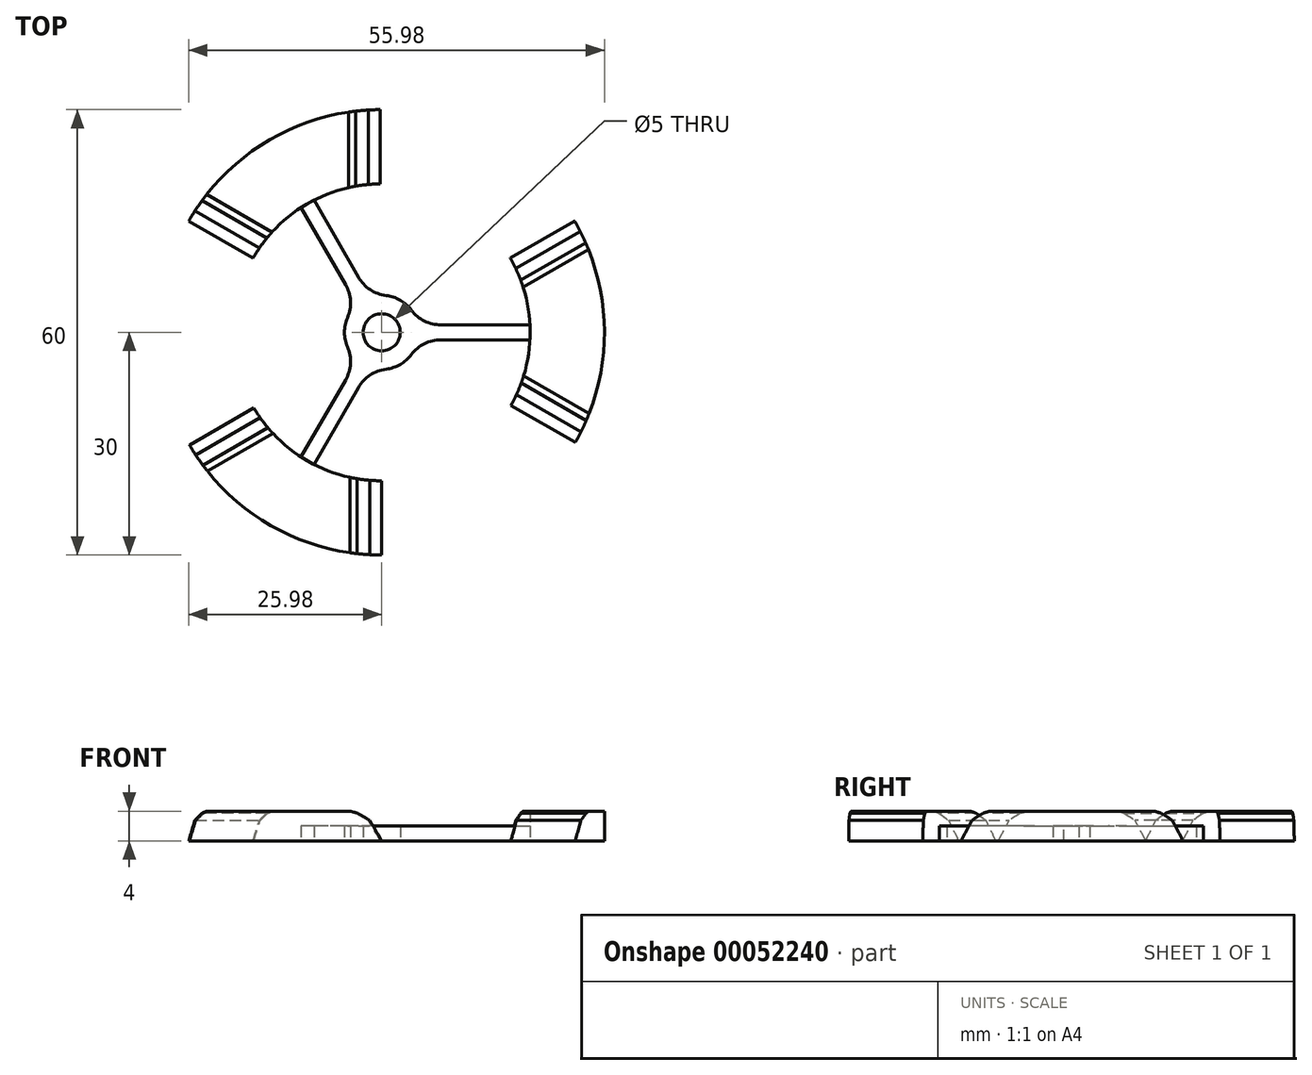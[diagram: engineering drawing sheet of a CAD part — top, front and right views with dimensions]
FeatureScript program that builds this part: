
annotation { "Feature Type Name" : "Feature", "Feature Type Description" : "" }
export const myFeature = defineFeature(function(context is Context, id is Id, definition is map)
    precondition{}
    {
        {
            var Q0;
            Q0=qCreatedBy(makeId("Top.planeOp"),FACE);
            var sketch = newSketch(context, id + "F0", { "sketchPlane" : qUnion([Q0])});
            skCircle(sketch, "E0", {"center": v(0, 0) * mm, "radius": 30 * mm});
            skCircle(sketch, "E1", {"center": v(0, 0) * mm, "radius": 20 * mm});
            skLineSegment(sketch, "E2", {"start": v(0, 20) * mm, "end": v(0, 30) * mm});
            skLineSegment(sketch, "E3", {"start": v(-17.32, -10) * mm, "end": v(-25.98, -15) * mm});
            skLineSegment(sketch, "E4", {"start": v(17.32, -10) * mm, "end": v(25.98, -15) * mm});
            skLineSegment(sketch, "E5", {"start": v(0, -20) * mm, "end": v(0, -30) * mm});
            skLineSegment(sketch, "E6", {"start": v(-17.32, 10) * mm, "end": v(-25.98, 15) * mm});
            skLineSegment(sketch, "E7", {"start": v(17.32, 10) * mm, "end": v(25.98, 15) * mm});
            skLineSegment(sketch, "E8", {"start": v(0, 0) * mm, "end": v(-10, 17.32) * mm, "construction": true});
            skLineSegment(sketch, "E9", {"start": v(0, 0) * mm, "end": v(-10, -17.32) * mm, "construction": true});
            skLineSegment(sketch, "E10", {"start": v(0, 0) * mm, "end": v(20, 0) * mm, "construction": true});
            skCircle(sketch, "E11", {"center": v(0, 0) * mm, "radius": 5 * mm});
            skLineSegment(sketch, "E12.0", {"start": v(-1.58, 4.74) * mm, "end": v(-9.12, 17.8) * mm});
            skLineSegment(sketch, "E13.MirrorCS", {"start": v(-3.32, 3.74) * mm, "end": v(-10.85, 16.8) * mm});
            skLineSegment(sketch, "E14.0", {"start": v(-3.32, -3.74) * mm, "end": v(-10.87, -16.82) * mm});
            skLineSegment(sketch, "E15.MirrorCS", {"start": v(-1.58, -4.74) * mm, "end": v(-9.13, -17.82) * mm});
            skLineSegment(sketch, "E16.0", {"start": v(4.9, -1) * mm, "end": v(20, -1) * mm});
            skLineSegment(sketch, "E17.MirrorCS", {"start": v(4.9, 1) * mm, "end": v(20, 1) * mm});
            skCircle(sketch, "E18", {"center": v(0, 0) * mm, "radius": 2.5 * mm});
            skSolve(sketch);
        }
        {
            var Q0;
            {var subQ0=sQuery(id+"F0.wireOp",EDGE,"E14.0");var subQ1=sQuery(id+"F0.wireOp",EDGE,"E1");var subQ2=makeQuery(id+"F0.imprint","INTERSECT",VERTEX,{"derivedFrom":[subQ1,subQ0]});Q0=makeQuery(id+"F0.imprint","IMPRINT",FACE,{"disambiguationData":[TD([[makeQuery(id+"F0.imprint","IMPRINT",EDGE,{"disambiguationData":[TD([[subQ2,-1.0]])],"derivedFrom":subQ1}),1.0]])]});}
            var Q1;
            {var subQ0=sQuery(id+"F0.wireOp",EDGE,"E12.0");Q1=makeQuery(id+"F0.imprint","IMPRINT",FACE,{"disambiguationData":[TD([[makeQuery(id+"F0.imprint","IMPRINT",EDGE,{"derivedFrom":subQ0}),1.0]])]});}
            var Q2;
            {var subQ0=sQuery(id+"F0.wireOp",EDGE,"E17.MirrorCS");var subQ1=sQuery(id+"F0.wireOp",EDGE,"E1");var subQ2=makeQuery(id+"F0.imprint","INTERSECT",VERTEX,{"derivedFrom":[subQ1,subQ0]});Q2=makeQuery(id+"F0.imprint","IMPRINT",FACE,{"disambiguationData":[TD([[makeQuery(id+"F0.imprint","IMPRINT",EDGE,{"disambiguationData":[TD([[subQ2,1.0]])],"derivedFrom":subQ1}),1.0]])]});}
            var Q3;
            {var subQ0=sQuery(id+"F0.wireOp",EDGE,"E11");var subQ4=makeQuery(id+"F0.imprint","INTERSECT",VERTEX,{"derivedFrom":[subQ0,sQuery(id+"F0.wireOp",EDGE,"E12.0")]});Q3=makeQuery(id+"F0.imprint","IMPRINT",FACE,{"disambiguationData":[TD([[makeQuery(id+"F0.imprint","IMPRINT",EDGE,{"disambiguationData":[TD([[subQ4,1.0]])],"derivedFrom":subQ0}),1.0]])]});}
            extrude(context, id + "F1", {"entities" : qUnion([Q0, Q1, Q2, Q3]), "depth" : 2 * mm});
        }
        {
            var Q0;
            {var subQ4=sQuery(id+"F0.wireOp",EDGE,"E2");Q0=makeQuery(id+"F0.imprint","IMPRINT",FACE,{"disambiguationData":[TD([[makeQuery(id+"F0.imprint","IMPRINT",EDGE,{"derivedFrom":subQ4}),1.0]])]});}
            var Q1;
            {var subQ4=sQuery(id+"F0.wireOp",EDGE,"E4");Q1=makeQuery(id+"F0.imprint","IMPRINT",FACE,{"disambiguationData":[TD([[makeQuery(id+"F0.imprint","IMPRINT",EDGE,{"derivedFrom":subQ4}),1.0]])]});}
            var Q2;
            {var subQ4=sQuery(id+"F0.wireOp",EDGE,"E3");Q2=makeQuery(id+"F0.imprint","IMPRINT",FACE,{"disambiguationData":[TD([[makeQuery(id+"F0.imprint","IMPRINT",EDGE,{"derivedFrom":subQ4}),1.0]])]});}
            extrude(context, id + "F2", {"entities" : qUnion([Q0, Q1, Q2]), "operationType" : NewBodyOperationType.ADD, "depth" : 4 * mm});
        }
        {
            var Q0;
            Q0=makeQuery(id+"F1.opExtrude","SWEPT_EDGE",EDGE,{"disambiguationData":[OSD([sQuery(id+"F0.wireOp",EDGE,"E1"),sQuery(id+"F0.wireOp",EDGE,"E12.0")])]});
            var Q1;
            Q1=makeQuery(id+"F1.opExtrude","SWEPT_EDGE",EDGE,{"disambiguationData":[OSD([sQuery(id+"F0.wireOp",EDGE,"E1"),sQuery(id+"F0.wireOp",EDGE,"E13.MirrorCS")])]});
            var Q2;
            Q2=makeQuery(id+"F1.opExtrude","SWEPT_EDGE",EDGE,{"disambiguationData":[OSD([sQuery(id+"F0.wireOp",EDGE,"E1"),sQuery(id+"F0.wireOp",EDGE,"E17.MirrorCS")])]});
            var Q3;
            Q3=makeQuery(id+"F1.opExtrude","SWEPT_EDGE",EDGE,{"disambiguationData":[OSD([sQuery(id+"F0.wireOp",EDGE,"E1"),sQuery(id+"F0.wireOp",EDGE,"E16.0")])]});
            var Q4;
            Q4=makeQuery(id+"F1.opExtrude","SWEPT_EDGE",EDGE,{"disambiguationData":[OSD([sQuery(id+"F0.wireOp",EDGE,"E1"),sQuery(id+"F0.wireOp",EDGE,"E14.0")])]});
            var Q5;
            Q5=makeQuery(id+"F1.opExtrude","SWEPT_EDGE",EDGE,{"disambiguationData":[OSD([sQuery(id+"F0.wireOp",EDGE,"E1"),sQuery(id+"F0.wireOp",EDGE,"E15.MirrorCS")])]});
            var Q6;
            Q6=makeQuery(id+"F1.opExtrude","SWEPT_EDGE",EDGE,{"disambiguationData":[OSD([sQuery(id+"F0.wireOp",EDGE,"E11"),sQuery(id+"F0.wireOp",EDGE,"E12.0")])]});
            var Q7;
            Q7=makeQuery(id+"F1.opExtrude","SWEPT_EDGE",EDGE,{"disambiguationData":[OSD([sQuery(id+"F0.wireOp",EDGE,"E11"),sQuery(id+"F0.wireOp",EDGE,"E17.MirrorCS")])]});
            var Q8;
            Q8=makeQuery(id+"F1.opExtrude","SWEPT_EDGE",EDGE,{"disambiguationData":[OSD([sQuery(id+"F0.wireOp",EDGE,"E11"),sQuery(id+"F0.wireOp",EDGE,"E13.MirrorCS")])]});
            var Q9;
            Q9=makeQuery(id+"F1.opExtrude","SWEPT_EDGE",EDGE,{"disambiguationData":[OSD([sQuery(id+"F0.wireOp",EDGE,"E11"),sQuery(id+"F0.wireOp",EDGE,"E14.0")])]});
            var Q10;
            Q10=makeQuery(id+"F1.opExtrude","SWEPT_EDGE",EDGE,{"disambiguationData":[OSD([sQuery(id+"F0.wireOp",EDGE,"E11"),sQuery(id+"F0.wireOp",EDGE,"E15.MirrorCS")])]});
            var Q11;
            Q11=makeQuery(id+"F1.opExtrude","SWEPT_EDGE",EDGE,{"disambiguationData":[OSD([sQuery(id+"F0.wireOp",EDGE,"E11"),sQuery(id+"F0.wireOp",EDGE,"E16.0")])]});
            fillet(context, id + "F3", {"entities" : qUnion([Q0, Q1, Q2, Q3, Q4, Q5, Q6, Q7, Q8, Q9, Q10, Q11]), "radius" : 5 * mm, "tangentPropagation" : true, "allowEdgeOverflow" : false});
        }
        {
            var Q0;
            Q0=makeQuery(id+"F2.opExtrude","CAP_EDGE",EDGE,{"disambiguationData":[OSD([sQuery(id+"F0.wireOp",EDGE,"E3")])],"isStart":false});
            var Q1;
            Q1=makeQuery(id+"F2.opExtrude","CAP_EDGE",EDGE,{"disambiguationData":[OSD([sQuery(id+"F0.wireOp",EDGE,"E2")])],"isStart":false});
            var Q2;
            Q2=makeQuery(id+"F2.opExtrude","CAP_EDGE",EDGE,{"disambiguationData":[OSD([sQuery(id+"F0.wireOp",EDGE,"E4")])],"isStart":false});
            chamfer(context, id + "F4", {"entities" : qUnion([Q0, Q1, Q2]), "chamferType" : ChamferType.OFFSET_ANGLE, "width" : 2.5 * mm, "oppositeDirection" : false, "angle" : 60 * degree, "tangentPropagation" : true});
        }
        {
            var Q0;
            Q0=makeQuery(id+"F2.opExtrude","CAP_EDGE",EDGE,{"disambiguationData":[OSD([sQuery(id+"F0.wireOp",EDGE,"E7")])],"isStart":false});
            var Q1;
            Q1=makeQuery(id+"F2.opExtrude","CAP_EDGE",EDGE,{"disambiguationData":[OSD([sQuery(id+"F0.wireOp",EDGE,"E6")])],"isStart":false});
            var Q2;
            Q2=makeQuery(id+"F2.opExtrude","CAP_EDGE",EDGE,{"disambiguationData":[OSD([sQuery(id+"F0.wireOp",EDGE,"E5")])],"isStart":false});
            chamfer(context, id + "F5", {"entities" : qUnion([Q0, Q1, Q2]), "chamferType" : ChamferType.OFFSET_ANGLE, "width" : 4 * mm, "oppositeDirection" : false, "angle" : 30 * degree, "tangentPropagation" : true});
        }
        {
            var Q0;
            {var subQ0=sQuery(id+"F0.wireOp",EDGE,"E6");Q0=makeQuery(id+"F5.opChamfer","BLEND_EDGE",EDGE,{"blendedFrom":[makeQuery(id+"F2.opExtrude","CAP_EDGE",EDGE,{"disambiguationData":[OSD([subQ0])],"isStart":false}),makeQuery(id+"F2.opExtrude","CAP_FACE",FACE,{"disambiguationData":[OSD([sQuery(id+"F0.wireOp",EDGE,"E0"),sQuery(id+"F0.wireOp",EDGE,"E1"),sQuery(id+"F0.wireOp",EDGE,"E2"),subQ0])],"isStart":false})],"blendedInto":[makeQuery(id+"F2.opExtrude","CAP_FACE",FACE,{"disambiguationData":[OSD([sQuery(id+"F0.wireOp",EDGE,"E0"),sQuery(id+"F0.wireOp",EDGE,"E1"),sQuery(id+"F0.wireOp",EDGE,"E2"),subQ0])],"isStart":false})]});}
            var Q1;
            {var subQ0=sQuery(id+"F0.wireOp",EDGE,"E2");Q1=makeQuery(id+"F4.opChamfer","BLEND_EDGE",EDGE,{"blendedFrom":[makeQuery(id+"F2.opExtrude","CAP_EDGE",EDGE,{"disambiguationData":[OSD([subQ0])],"isStart":false}),makeQuery(id+"F2.opExtrude","CAP_FACE",FACE,{"disambiguationData":[OSD([sQuery(id+"F0.wireOp",EDGE,"E0"),sQuery(id+"F0.wireOp",EDGE,"E1"),subQ0,sQuery(id+"F0.wireOp",EDGE,"E6")])],"isStart":false})],"blendedInto":[makeQuery(id+"F2.opExtrude","CAP_FACE",FACE,{"disambiguationData":[OSD([sQuery(id+"F0.wireOp",EDGE,"E0"),sQuery(id+"F0.wireOp",EDGE,"E1"),subQ0,sQuery(id+"F0.wireOp",EDGE,"E6")])],"isStart":false})]});}
            var Q2;
            {var subQ0=sQuery(id+"F0.wireOp",EDGE,"E7");Q2=makeQuery(id+"F5.opChamfer","BLEND_EDGE",EDGE,{"blendedFrom":[makeQuery(id+"F2.opExtrude","CAP_EDGE",EDGE,{"disambiguationData":[OSD([subQ0])],"isStart":false}),makeQuery(id+"F2.opExtrude","CAP_FACE",FACE,{"disambiguationData":[OSD([sQuery(id+"F0.wireOp",EDGE,"E0"),sQuery(id+"F0.wireOp",EDGE,"E1"),sQuery(id+"F0.wireOp",EDGE,"E4"),subQ0])],"isStart":false})],"blendedInto":[makeQuery(id+"F2.opExtrude","CAP_FACE",FACE,{"disambiguationData":[OSD([sQuery(id+"F0.wireOp",EDGE,"E0"),sQuery(id+"F0.wireOp",EDGE,"E1"),sQuery(id+"F0.wireOp",EDGE,"E4"),subQ0])],"isStart":false})]});}
            var Q3;
            {var subQ0=sQuery(id+"F0.wireOp",EDGE,"E4");Q3=makeQuery(id+"F4.opChamfer","BLEND_EDGE",EDGE,{"blendedFrom":[makeQuery(id+"F2.opExtrude","CAP_EDGE",EDGE,{"disambiguationData":[OSD([subQ0])],"isStart":false}),makeQuery(id+"F2.opExtrude","CAP_FACE",FACE,{"disambiguationData":[OSD([sQuery(id+"F0.wireOp",EDGE,"E0"),sQuery(id+"F0.wireOp",EDGE,"E1"),subQ0,sQuery(id+"F0.wireOp",EDGE,"E7")])],"isStart":false})],"blendedInto":[makeQuery(id+"F2.opExtrude","CAP_FACE",FACE,{"disambiguationData":[OSD([sQuery(id+"F0.wireOp",EDGE,"E0"),sQuery(id+"F0.wireOp",EDGE,"E1"),subQ0,sQuery(id+"F0.wireOp",EDGE,"E7")])],"isStart":false})]});}
            var Q4;
            {var subQ0=sQuery(id+"F0.wireOp",EDGE,"E5");Q4=makeQuery(id+"F5.opChamfer","BLEND_EDGE",EDGE,{"blendedFrom":[makeQuery(id+"F2.opExtrude","CAP_EDGE",EDGE,{"disambiguationData":[OSD([subQ0])],"isStart":false}),makeQuery(id+"F2.opExtrude","CAP_FACE",FACE,{"disambiguationData":[OSD([sQuery(id+"F0.wireOp",EDGE,"E0"),sQuery(id+"F0.wireOp",EDGE,"E1"),sQuery(id+"F0.wireOp",EDGE,"E3"),subQ0])],"isStart":false})],"blendedInto":[makeQuery(id+"F2.opExtrude","CAP_FACE",FACE,{"disambiguationData":[OSD([sQuery(id+"F0.wireOp",EDGE,"E0"),sQuery(id+"F0.wireOp",EDGE,"E1"),sQuery(id+"F0.wireOp",EDGE,"E3"),subQ0])],"isStart":false})]});}
            var Q5;
            {var subQ0=sQuery(id+"F0.wireOp",EDGE,"E3");Q5=makeQuery(id+"F4.opChamfer","BLEND_EDGE",EDGE,{"blendedFrom":[makeQuery(id+"F2.opExtrude","CAP_EDGE",EDGE,{"disambiguationData":[OSD([subQ0])],"isStart":false}),makeQuery(id+"F2.opExtrude","CAP_FACE",FACE,{"disambiguationData":[OSD([sQuery(id+"F0.wireOp",EDGE,"E0"),sQuery(id+"F0.wireOp",EDGE,"E1"),subQ0,sQuery(id+"F0.wireOp",EDGE,"E5")])],"isStart":false})],"blendedInto":[makeQuery(id+"F2.opExtrude","CAP_FACE",FACE,{"disambiguationData":[OSD([sQuery(id+"F0.wireOp",EDGE,"E0"),sQuery(id+"F0.wireOp",EDGE,"E1"),subQ0,sQuery(id+"F0.wireOp",EDGE,"E5")])],"isStart":false})]});}
            chamfer(context, id + "F6", {"entities" : qUnion([Q0, Q1, Q2, Q3, Q4, Q5]), "width" : 2.5 * mm, "tangentPropagation" : true});
        }
        {
            var Q0;
            {var subQ0=sQuery(id+"F0.wireOp",EDGE,"E2");var subQ1=makeQuery(id+"F2.opExtrude","CAP_FACE",FACE,{"disambiguationData":[OSD([sQuery(id+"F0.wireOp",EDGE,"E0"),sQuery(id+"F0.wireOp",EDGE,"E1"),subQ0,sQuery(id+"F0.wireOp",EDGE,"E6")])],"isStart":false});Q0=makeQuery(id+"F6.opChamfer","BLEND_EDGE",EDGE,{"blendedFrom":[makeQuery(id+"F4.opChamfer","BLEND_EDGE",EDGE,{"blendedFrom":[makeQuery(id+"F2.opExtrude","CAP_EDGE",EDGE,{"disambiguationData":[OSD([subQ0])],"isStart":false}),subQ1],"blendedInto":[subQ1]}),subQ1],"blendedInto":[subQ1]});}
            var Q1;
            {var subQ0=sQuery(id+"F0.wireOp",EDGE,"E6");var subQ1=makeQuery(id+"F2.opExtrude","CAP_FACE",FACE,{"disambiguationData":[OSD([sQuery(id+"F0.wireOp",EDGE,"E0"),sQuery(id+"F0.wireOp",EDGE,"E1"),sQuery(id+"F0.wireOp",EDGE,"E2"),subQ0])],"isStart":false});Q1=makeQuery(id+"F6.opChamfer","BLEND_EDGE",EDGE,{"blendedFrom":[makeQuery(id+"F5.opChamfer","BLEND_EDGE",EDGE,{"blendedFrom":[makeQuery(id+"F2.opExtrude","CAP_EDGE",EDGE,{"disambiguationData":[OSD([subQ0])],"isStart":false}),subQ1],"blendedInto":[subQ1]}),subQ1],"blendedInto":[subQ1]});}
            var Q2;
            {var subQ0=sQuery(id+"F0.wireOp",EDGE,"E7");var subQ1=makeQuery(id+"F2.opExtrude","CAP_FACE",FACE,{"disambiguationData":[OSD([sQuery(id+"F0.wireOp",EDGE,"E0"),sQuery(id+"F0.wireOp",EDGE,"E1"),sQuery(id+"F0.wireOp",EDGE,"E4"),subQ0])],"isStart":false});Q2=makeQuery(id+"F6.opChamfer","BLEND_EDGE",EDGE,{"blendedFrom":[makeQuery(id+"F5.opChamfer","BLEND_EDGE",EDGE,{"blendedFrom":[makeQuery(id+"F2.opExtrude","CAP_EDGE",EDGE,{"disambiguationData":[OSD([subQ0])],"isStart":false}),subQ1],"blendedInto":[subQ1]}),subQ1],"blendedInto":[subQ1]});}
            var Q3;
            {var subQ0=sQuery(id+"F0.wireOp",EDGE,"E4");var subQ1=makeQuery(id+"F2.opExtrude","CAP_FACE",FACE,{"disambiguationData":[OSD([sQuery(id+"F0.wireOp",EDGE,"E0"),sQuery(id+"F0.wireOp",EDGE,"E1"),subQ0,sQuery(id+"F0.wireOp",EDGE,"E7")])],"isStart":false});Q3=makeQuery(id+"F6.opChamfer","BLEND_EDGE",EDGE,{"blendedFrom":[makeQuery(id+"F4.opChamfer","BLEND_EDGE",EDGE,{"blendedFrom":[makeQuery(id+"F2.opExtrude","CAP_EDGE",EDGE,{"disambiguationData":[OSD([subQ0])],"isStart":false}),subQ1],"blendedInto":[subQ1]}),subQ1],"blendedInto":[subQ1]});}
            var Q4;
            {var subQ0=sQuery(id+"F0.wireOp",EDGE,"E5");var subQ1=makeQuery(id+"F2.opExtrude","CAP_FACE",FACE,{"disambiguationData":[OSD([sQuery(id+"F0.wireOp",EDGE,"E0"),sQuery(id+"F0.wireOp",EDGE,"E1"),sQuery(id+"F0.wireOp",EDGE,"E3"),subQ0])],"isStart":false});Q4=makeQuery(id+"F6.opChamfer","BLEND_EDGE",EDGE,{"blendedFrom":[makeQuery(id+"F5.opChamfer","BLEND_EDGE",EDGE,{"blendedFrom":[makeQuery(id+"F2.opExtrude","CAP_EDGE",EDGE,{"disambiguationData":[OSD([subQ0])],"isStart":false}),subQ1],"blendedInto":[subQ1]}),subQ1],"blendedInto":[subQ1]});}
            var Q5;
            {var subQ0=sQuery(id+"F0.wireOp",EDGE,"E3");var subQ1=makeQuery(id+"F2.opExtrude","CAP_FACE",FACE,{"disambiguationData":[OSD([sQuery(id+"F0.wireOp",EDGE,"E0"),sQuery(id+"F0.wireOp",EDGE,"E1"),subQ0,sQuery(id+"F0.wireOp",EDGE,"E5")])],"isStart":false});Q5=makeQuery(id+"F6.opChamfer","BLEND_EDGE",EDGE,{"blendedFrom":[makeQuery(id+"F4.opChamfer","BLEND_EDGE",EDGE,{"blendedFrom":[makeQuery(id+"F2.opExtrude","CAP_EDGE",EDGE,{"disambiguationData":[OSD([subQ0])],"isStart":false}),subQ1],"blendedInto":[subQ1]}),subQ1],"blendedInto":[subQ1]});}
            chamfer(context, id + "F7", {"entities" : qUnion([Q0, Q1, Q2, Q3, Q4, Q5]), "width" : 2 * mm, "tangentPropagation" : true});
        }
    });
